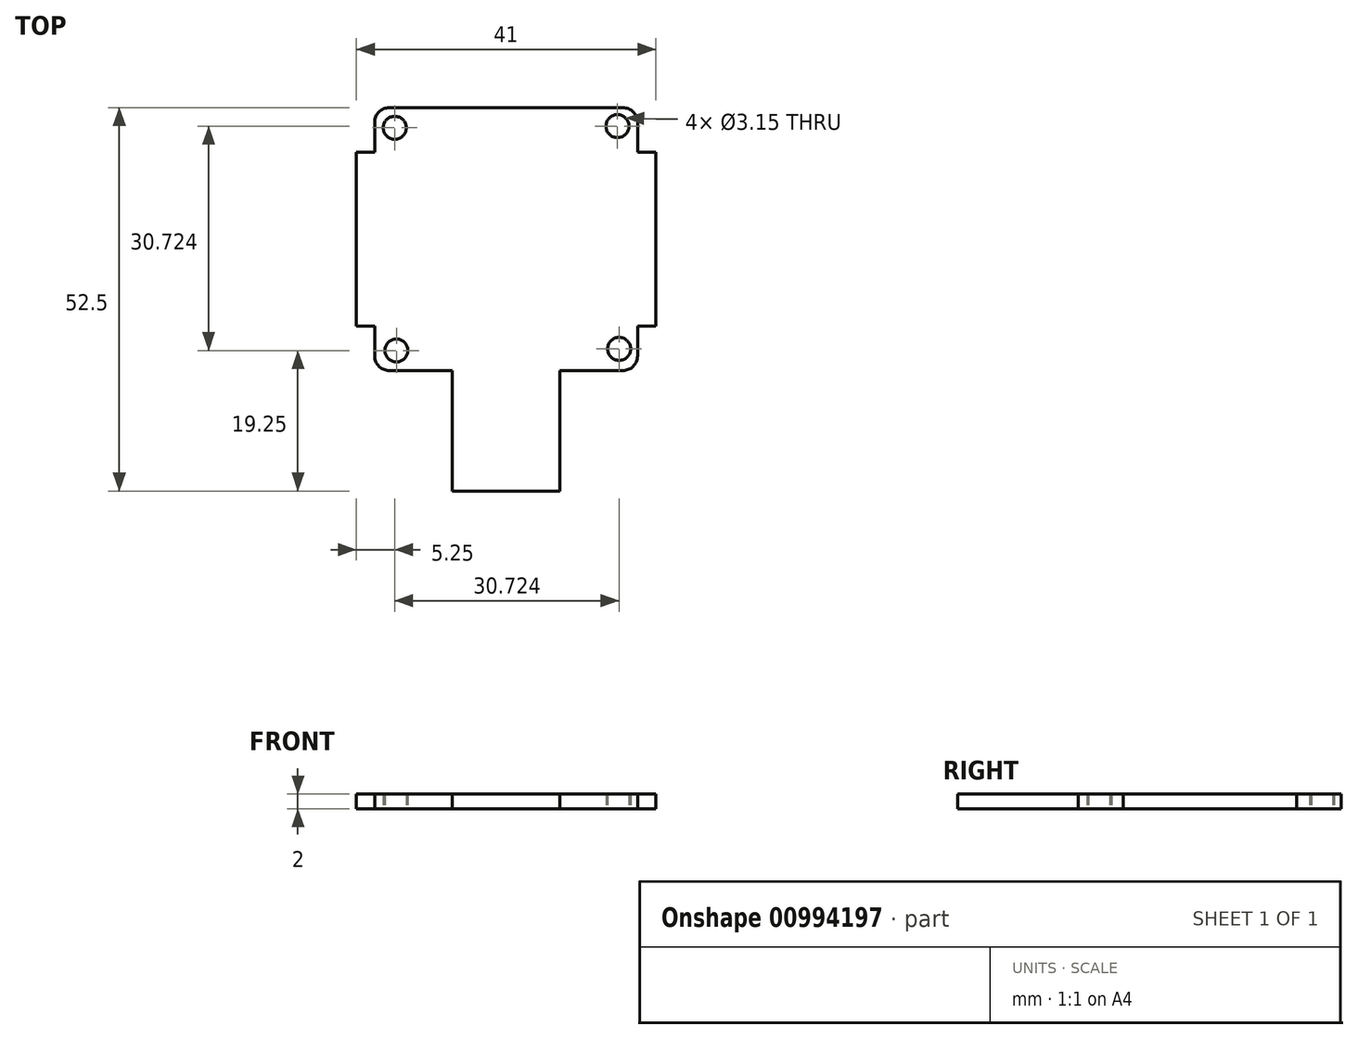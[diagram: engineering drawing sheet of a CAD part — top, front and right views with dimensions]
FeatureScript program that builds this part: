
annotation { "Feature Type Name" : "Feature", "Feature Type Description" : "" }
export const myFeature = defineFeature(function(context is Context, id is Id, definition is map)
    precondition{}
    {
        {
            var Q0;
            Q0=qCreatedBy(makeId("Top.planeOp"),FACE);
            var sketch = newSketch(context, id + "F0", { "sketchPlane" : qUnion([Q0])});
            skCircle(sketch, "E0.0", {"center": v(-15.03, -15.25) * mm, "radius": 1.57 * mm});
            skCircle(sketch, "E1.0", {"center": v(15.47, -15.03) * mm, "radius": 1.57 * mm});
            skCircle(sketch, "E2.0", {"center": v(15.25, 15.47) * mm, "radius": 1.57 * mm});
            skCircle(sketch, "E3.0", {"center": v(-15.25, 15.25) * mm, "radius": 1.57 * mm});
            skLineSegment(sketch, "E4.bottom", {"start": v(-16, -18) * mm, "end": v(16, -18) * mm});
            skLineSegment(sketch, "E4.top", {"start": v(-16, 18) * mm, "end": v(16, 18) * mm});
            skLineSegment(sketch, "E4.left", {"start": v(-18, -16) * mm, "end": v(-18, 16) * mm});
            skLineSegment(sketch, "E4.right", {"start": v(18, -16) * mm, "end": v(18, 16) * mm});
            skPoint(sketch, "E5", {"position": v(0, -18) * mm});
            skPoint(sketch, "E6", {"position": v(-18, 0) * mm});
            skPoint(sketch, "E7.visualSharp", {"position": v(-18, -18) * mm});
            skArc(sketch, "E7.filletArc", {"start": v(-18, -16) * mm, "mid": v(-17.41, -17.41) * mm, "end": v(-16, -18) * mm});
            skPoint(sketch, "E8.visualSharp", {"position": v(18, -18) * mm});
            skArc(sketch, "E8.filletArc", {"start": v(16, -18) * mm, "mid": v(17.41, -17.41) * mm, "end": v(18, -16) * mm});
            skPoint(sketch, "E9.visualSharp", {"position": v(18, 18) * mm});
            skArc(sketch, "E9.filletArc", {"start": v(18, 16) * mm, "mid": v(17.41, 17.41) * mm, "end": v(16, 18) * mm});
            skPoint(sketch, "E10.visualSharp", {"position": v(-18, 18) * mm});
            skArc(sketch, "E10.filletArc", {"start": v(-16, 18) * mm, "mid": v(-17.41, 17.41) * mm, "end": v(-18, 16) * mm});
            skLineSegment(sketch, "E11.bottom", {"start": v(-7.35, -18) * mm, "end": v(7.35, -18) * mm});
            skLineSegment(sketch, "E11.top", {"start": v(-7.35, -34.5) * mm, "end": v(7.35, -34.5) * mm});
            skLineSegment(sketch, "E11.left", {"start": v(-7.35, -18) * mm, "end": v(-7.35, -34.5) * mm});
            skLineSegment(sketch, "E11.right", {"start": v(7.35, -18) * mm, "end": v(7.35, -34.5) * mm});
            skLineSegment(sketch, "E12.bottom", {"start": v(-18, 11.88) * mm, "end": v(-20.5, 11.88) * mm});
            skLineSegment(sketch, "E12.top", {"start": v(-18, -11.88) * mm, "end": v(-20.5, -11.88) * mm});
            skLineSegment(sketch, "E12.left", {"start": v(-18, 11.88) * mm, "end": v(-18, -11.88) * mm});
            skLineSegment(sketch, "E12.right", {"start": v(-20.5, 11.88) * mm, "end": v(-20.5, -11.88) * mm});
            skLineSegment(sketch, "E13.MirrorCS", {"start": v(17.98, 12.5) * mm, "end": v(17.98, -11.28) * mm});
            skLineSegment(sketch, "E14", {"start": v(15.25, 15.47) * mm, "end": v(15.47, -15.03) * mm, "construction": true});
            skLineSegment(sketch, "E15", {"start": v(15.47, -15.03) * mm, "end": v(-15.03, -15.25) * mm, "construction": true});
            skLineSegment(sketch, "E16", {"start": v(-15.03, -15.25) * mm, "end": v(-15.25, 15.25) * mm, "construction": true});
            skLineSegment(sketch, "E17", {"start": v(-15.25, 15.25) * mm, "end": v(15.25, 15.47) * mm, "construction": true});
            skPoint(sketch, "E18", {"position": v(-15.14, 0) * mm});
            skPoint(sketch, "E19", {"position": v(0, 18) * mm});
            skPoint(sketch, "E20", {"position": v(0, 15.36) * mm});
            skLineSegment(sketch, "E21.MirrorCS", {"start": v(18, 11.88) * mm, "end": v(20.5, 11.88) * mm});
            skLineSegment(sketch, "E22.MirrorCS", {"start": v(20.5, 11.88) * mm, "end": v(20.5, -11.88) * mm});
            skLineSegment(sketch, "E23.MirrorCS", {"start": v(18, -11.88) * mm, "end": v(20.5, -11.88) * mm});
            skSolve(sketch);
        }
        {
            var Q0;
            Q0 = qSketchRegion(id + "F0", true);
            extrude(context, id + "F1", {"entities" : qUnion([Q0]), "depth" : 2 * mm, "offsetDistance" : 25 * mm});
        }
    });
